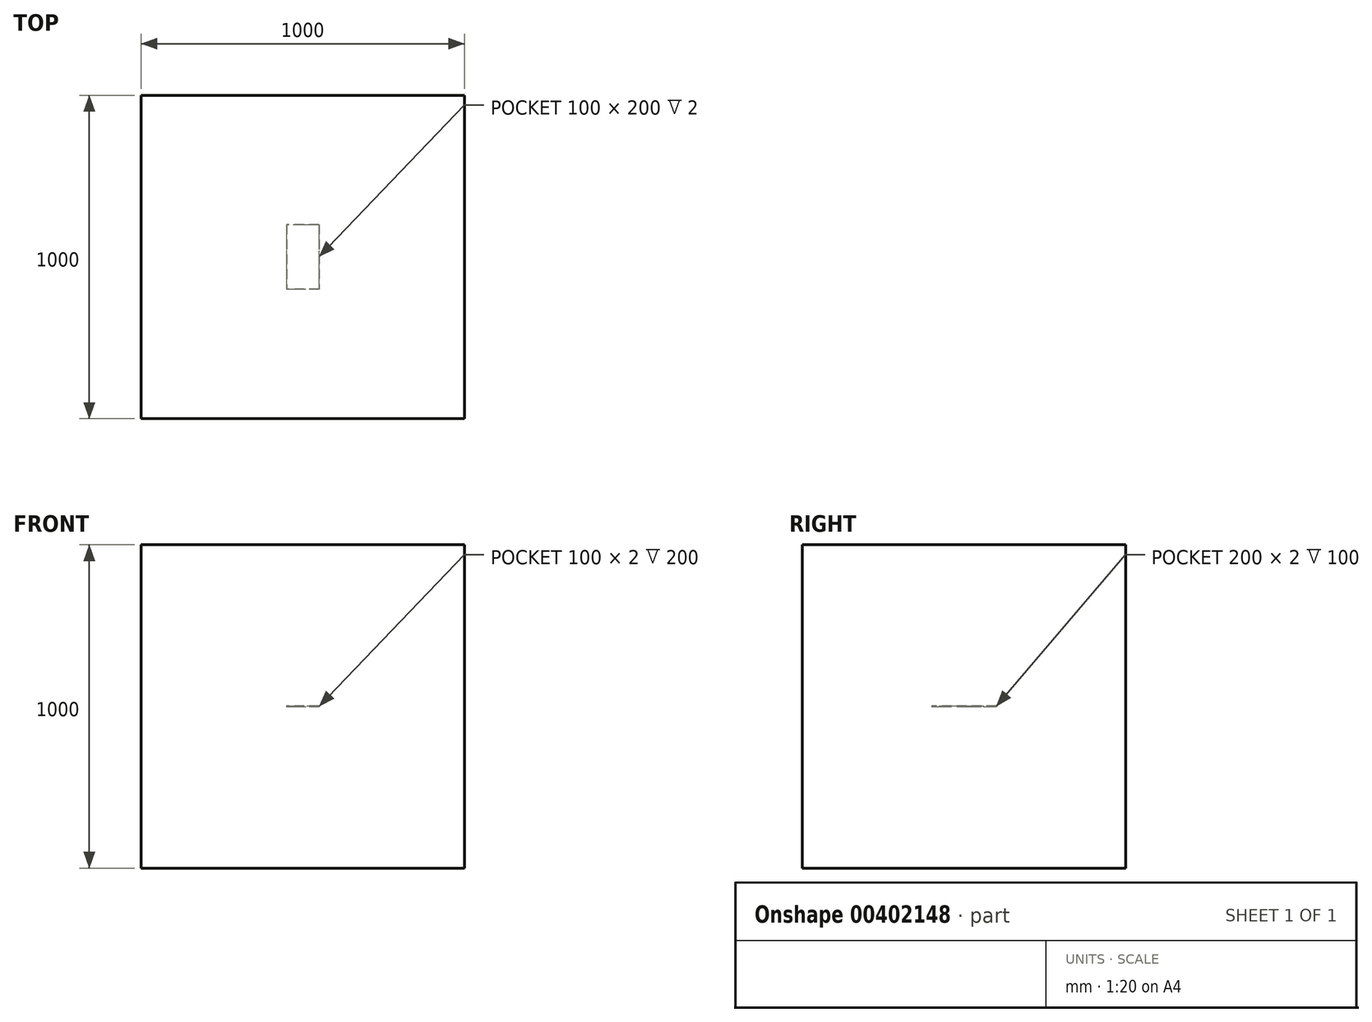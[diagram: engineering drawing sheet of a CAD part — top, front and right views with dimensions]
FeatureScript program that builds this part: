
annotation { "Feature Type Name" : "Feature", "Feature Type Description" : "" }
export const myFeature = defineFeature(function(context is Context, id is Id, definition is map)
    precondition{}
    {
        {
            var Q0;
            Q0=qCreatedBy(makeId("Top.planeOp"),FACE);
            var sketch = newSketch(context, id + "F0", { "sketchPlane" : qUnion([Q0])});
            skLineSegment(sketch, "E0.bottom", {"start": v(50, 100) * mm, "end": v(-50, 100) * mm});
            skLineSegment(sketch, "E0.top", {"start": v(50, -100) * mm, "end": v(-50, -100) * mm});
            skLineSegment(sketch, "E0.left", {"start": v(50, 100) * mm, "end": v(50, -100) * mm});
            skLineSegment(sketch, "E0.right", {"start": v(-50, 100) * mm, "end": v(-50, -100) * mm});
            skPoint(sketch, "E0.middle", {"position": v(0, 0) * mm});
            skSolve(sketch);
        }
        {
            var Q0;
            Q0 = qSketchRegion(id + "F0", true);
            var Q1;
            Q1 = qSketchRegion(id + "F2", true);
            extrude(context, id + "F1", {"entities" : qUnion([Q0, Q1]), "depth" : 1 * mm, "hasSecondDirection" : true, "secondDirectionOppositeDirection" : true, "secondDirectionDepth" : 1 * mm});
        }
        {
            var Q0;
            Q0=qCreatedBy(makeId("Top.planeOp"),FACE);
            var sketch = newSketch(context, id + "F2", { "sketchPlane" : qUnion([Q0])});
            skLineSegment(sketch, "E1.bottom", {"start": v(500, -500) * mm, "end": v(-500, -500) * mm});
            skLineSegment(sketch, "E1.top", {"start": v(500, 500) * mm, "end": v(-500, 500) * mm});
            skLineSegment(sketch, "E1.left", {"start": v(500, -500) * mm, "end": v(500, 500) * mm});
            skLineSegment(sketch, "E1.right", {"start": v(-500, -500) * mm, "end": v(-500, 500) * mm});
            skSolve(sketch);
        }
        {
            var Q0;
            Q0 = qSketchRegion(id + "F2", true);
            extrude(context, id + "F3", {"entities" : qUnion([Q0]), "depth" : 500 * mm, "hasSecondDirection" : true, "secondDirectionOppositeDirection" : true, "secondDirectionDepth" : 500 * mm});
        }
        {
            var Q0;
            Q0=makeQuery(id+"F1.opExtrude","SWEPT_BODY",BODY,{"disambiguationData":[OSD([sQuery(id+"F0.wireOp",EDGE,"E0.bottom"),sQuery(id+"F0.wireOp",EDGE,"E0.top"),sQuery(id+"F0.wireOp",EDGE,"E0.left"),sQuery(id+"F0.wireOp",EDGE,"E0.right")])]});
            var Q1;
            Q1=makeQuery(id+"F3.opExtrude","SWEPT_BODY",BODY,{"disambiguationData":[OSD([sQuery(id+"F2.wireOp",EDGE,"E1.bottom"),sQuery(id+"F2.wireOp",EDGE,"E1.top"),sQuery(id+"F2.wireOp",EDGE,"E1.left"),sQuery(id+"F2.wireOp",EDGE,"E1.right")])]});
            booleanBodies(context, id + "F4", {"operationType" : BooleanOperationType.SUBTRACTION, "tools" : qUnion([Q0]), "targets" : qUnion([Q1]), "keepTools" : true});
        }
    });
